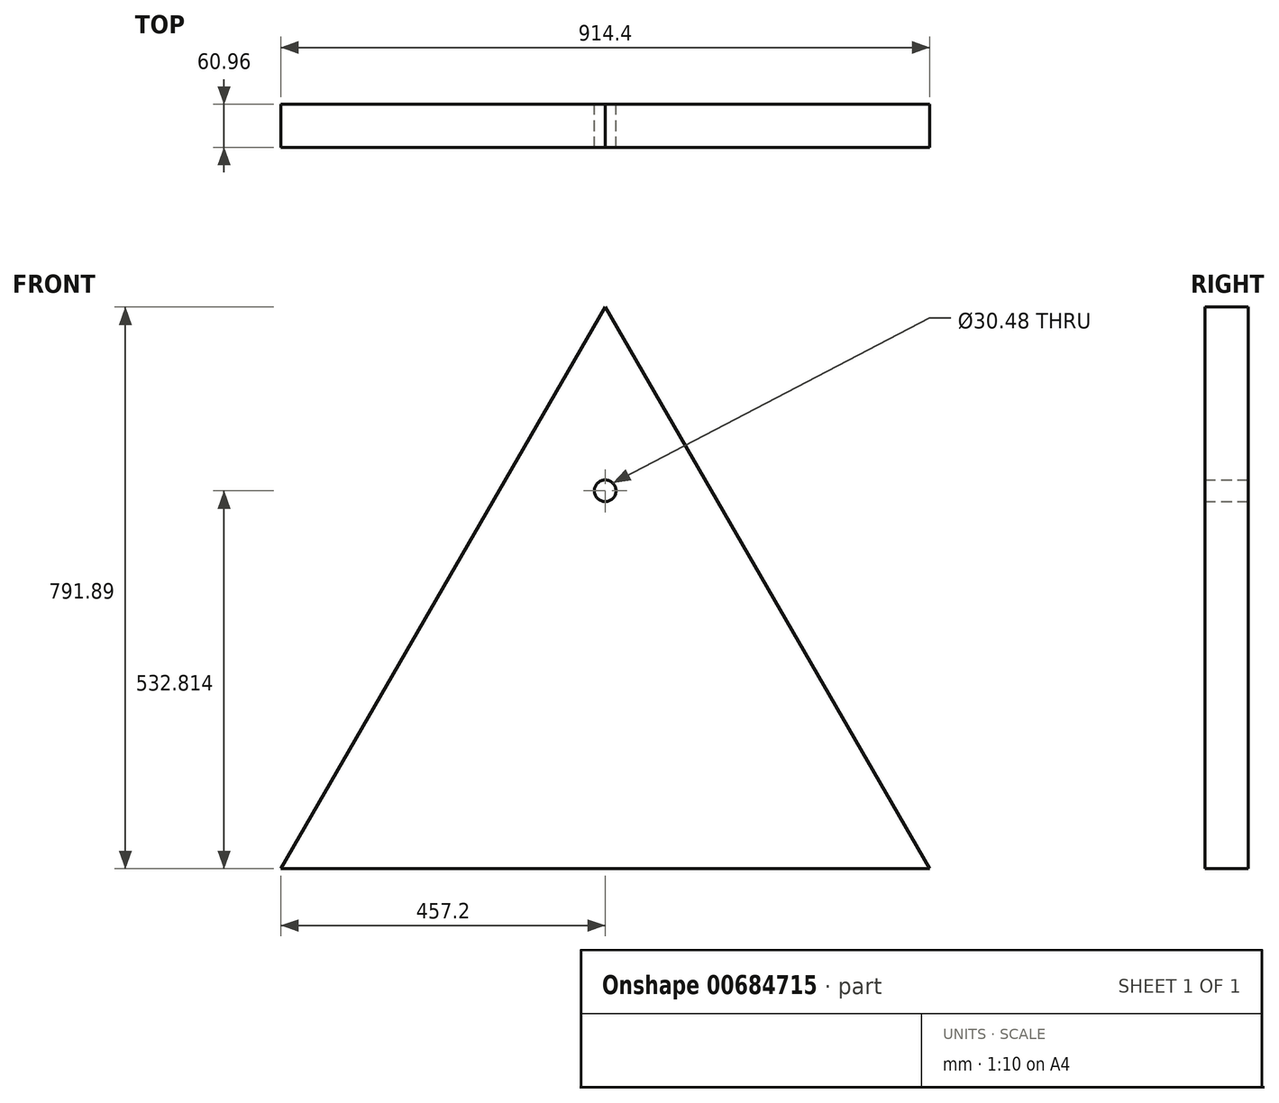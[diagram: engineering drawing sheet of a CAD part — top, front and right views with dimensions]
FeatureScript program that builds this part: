
annotation { "Feature Type Name" : "Feature", "Feature Type Description" : "" }
export const myFeature = defineFeature(function(context is Context, id is Id, definition is map)
    precondition{}
    {
        {
            var Q0;
            Q0=qCreatedBy(makeId("Front.planeOp"),FACE);
            var sketch = newSketch(context, id + "F0", { "sketchPlane" : qUnion([Q0])});
            skLineSegment(sketch, "E0", {"start": v(0, 0) * mm, "end": v(914.4, 0) * mm});
            skLineSegment(sketch, "E1", {"start": v(914.4, 0) * mm, "end": v(457.2, 791.9) * mm});
            skLineSegment(sketch, "E2", {"start": v(457.2, 791.9) * mm, "end": v(0, 0) * mm});
            skCircle(sketch, "E3", {"center": v(457.2, 532.81) * mm, "radius": 15.24 * mm});
            skSolve(sketch);
        }
        {
            var Q0;
            Q0 = qSketchRegion(id + "F0", true);
            extrude(context, id + "F1", {"entities" : qUnion([Q0]), "depth" : 60.96 * mm, "offsetDistance" : 30.48 * mm});
        }
        {
            var Q0;
            Q0 = qSketchRegion(id + "F0", true);
            extrude(context, id + "F2", {"entities" : qUnion([Q0]), "operationType" : NewBodyOperationType.ADD, "depth" : 30.48 * mm, "offsetDistance" : 30.48 * mm});
        }
    });
